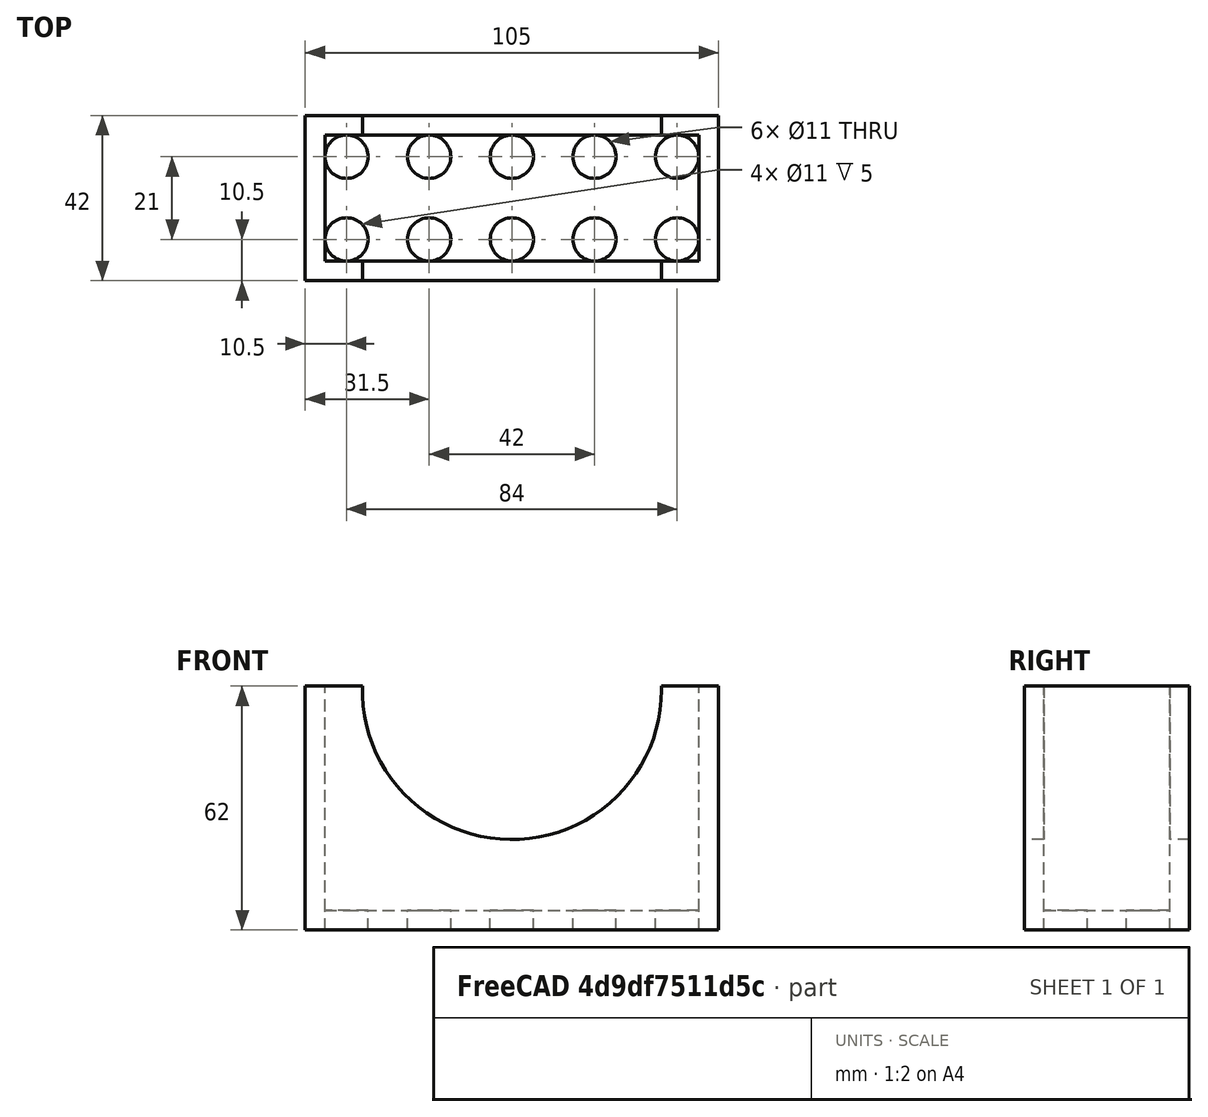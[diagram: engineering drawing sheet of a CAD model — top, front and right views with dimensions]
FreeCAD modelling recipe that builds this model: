
FCSTD DOCUMENT  (FreeCAD 0.18R16110 (Git))
Label: eppi-rack
License: All rights reserved
LicenseURL: http://en.wikipedia.org/wiki/All_rights_reserved
objects: Part::Cut×12, Part::Cylinder×11, Part::Box×2, Mesh::Feature×1
note: 25 computed .brp shape members not serialized (recipe doc carries the construction recipe); baked Part::Feature solids carry a one-line shape summary decoded from their .brp

FEATURE [Part::Cylinder] Cylinder  label="Zylinder"
  Angle = 360
  AttacherType = Attacher::AttachEngine3D
  Height = 5
  Placement = pos=(84,21,0) rot=(0,0,1;0rad)
  Radius = 5.5
  expr: Placement.Base.x = 21 * 4
  expr: Placement.Base.y = 21
  expr: Radius = 11 / 2
FEATURE [Part::Cylinder] Cylinder001  label="Zylinder001"
  Angle = 360
  AttacherType = Attacher::AttachEngine3D
  Height = 5
  Placement = pos=(21,0,0) rot=(0,0,1;0rad)
  Radius = 5.5
  expr: Radius = 11 / 2
FEATURE [Part::Cylinder] Cylinder002  label="Zylinder002"
  Angle = 360
  AttacherType = Attacher::AttachEngine3D
  Height = 5
  Placement = pos=(42,0,0) rot=(0,0,1;0rad)
  Radius = 5.5
  expr: Placement.Base.x = 21 * 2
  expr: Radius = 11 / 2
FEATURE [Part::Cylinder] Cylinder003  label="Zylinder003"
  Angle = 360
  AttacherType = Attacher::AttachEngine3D
  Height = 5
  Placement = pos=(84,0,0) rot=(0,0,1;0rad)
  Radius = 5.5
  expr: Placement.Base.x = 21 * 4
  expr: Radius = 11 / 2
FEATURE [Part::Cylinder] Cylinder004  label="Zylinder004"
  Angle = 360
  AttacherType = Attacher::AttachEngine3D
  Height = 5
  Placement = pos=(63,0,0) rot=(0,0,1;0rad)
  Radius = 5.5
  expr: Placement.Base.x = 21 * 3
  expr: Radius = 11 / 2
FEATURE [Part::Cylinder] Cylinder005  label="Zylinder005"
  Angle = 360
  AttacherType = Attacher::AttachEngine3D
  Height = 5
  Radius = 5.5
  expr: Radius = 11 / 2
FEATURE [Part::Cylinder] Cylinder006  label="Zylinder006"
  Angle = 360
  AttacherType = Attacher::AttachEngine3D
  Height = 5
  Placement = pos=(0,21,0) rot=(0,0,1;0rad)
  Radius = 5.5
  expr: Placement.Base.y = 21
  expr: Radius = 11 / 2
FEATURE [Part::Cylinder] Cylinder007  label="Zylinder007"
  Angle = 360
  AttacherType = Attacher::AttachEngine3D
  Height = 5
  Placement = pos=(21,21,0) rot=(0,0,1;0rad)
  Radius = 5.5
  expr: Placement.Base.x = 21
  expr: Placement.Base.y = 21
  expr: Radius = 11 / 2
FEATURE [Part::Cylinder] Cylinder008  label="Zylinder008"
  Angle = 360
  AttacherType = Attacher::AttachEngine3D
  Height = 5
  Placement = pos=(42,21,0) rot=(0,0,1;0rad)
  Radius = 5.5
  expr: Placement.Base.x = 21 * 2
  expr: Placement.Base.y = 21
  expr: Radius = 11 / 2
FEATURE [Part::Cylinder] Cylinder009  label="Zylinder009"
  Angle = 360
  AttacherType = Attacher::AttachEngine3D
  Height = 5
  Placement = pos=(63,21,0) rot=(0,0,1;0rad)
  Radius = 5.5
  expr: Placement.Base.x = 21 * 3
  expr: Placement.Base.y = 21
  expr: Radius = 11 / 2
FEATURE [Part::Box] Box001  label="Quader001"
  AttacherType = Attacher::AttachEngine3D
  Height = 62
  Length = 105
  Placement = pos=(-10.5,-10.5,0) rot=(0,0,1;0rad)
  Width = 42
FEATURE [Part::Box] Box002  label="Quader002"
  AttacherType = Attacher::AttachEngine3D
  Height = 62
  Length = 95
  Placement = pos=(-5.5,-5.5,5) rot=(0,0,1;0rad)
  Width = 32
FEATURE [Part::Cut] Cut
  Base = -> Box001
  Tool = -> Box002
FEATURE [Part::Cut] Cut001
  Base = -> Cut
  Tool = -> Cylinder009
FEATURE [Part::Cut] Cut002
  Base = -> Cut001
  Tool = -> Cylinder008
FEATURE [Part::Cut] Cut003
  Base = -> Cut002
  Tool = -> Cylinder007
FEATURE [Part::Cut] Cut004
  Base = -> Cut003
  Tool = -> Cylinder006
FEATURE [Part::Cut] Cut005
  Base = -> Cut004
  Tool = -> Cylinder005
FEATURE [Part::Cut] Cut006
  Base = -> Cut005
  Tool = -> Cylinder004
FEATURE [Part::Cut] Cut007
  Base = -> Cut006
  Tool = -> Cylinder003
FEATURE [Part::Cut] Cut008
  Base = -> Cut007
  Tool = -> Cylinder002
FEATURE [Part::Cut] Cut009
  Base = -> Cut008
  Tool = -> Cylinder001
FEATURE [Part::Cut] Cut010
  Base = -> Cut009
  Tool = -> Cylinder
FEATURE [Part::Cylinder] Cylinder010  label="Zylinder010"
  Angle = 360
  AttacherType = Attacher::AttachEngine3D
  Height = 60
  Placement = pos=(42,37,61) rot=(1,0,0;1.5708rad)
  Radius = 38
  expr: Placement.Base.x = -10.5 + 105 / 2
FEATURE [Part::Cut] Cut011  label="eppi-rack"
  Base = -> Cut010
  Tool = -> Cylinder010
FEATURE [Mesh::Feature] Mesh  label="eppi-rack(Meshed)"
